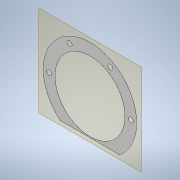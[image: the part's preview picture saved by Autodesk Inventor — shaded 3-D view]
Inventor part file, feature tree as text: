
AUTODESK INVENTOR PART (.ipt)
format: ipt  version: 2020 (Build 240168000, 168)  size: 113,664 bytes
history: native  units: mm
features: other x3, plane x1, extrude x1, sketch x1, reference x1
ambient origin geometry x8: Origin, YZ Plane, XZ Plane, XY Plane, X Axis, Y Axis, Z Axis, Center Point
bodies: 实体1 (feature_tree)
feature tree (7):
  plane  "工作平面1"
  extrude  "拉伸1"  [1 undecoded]
  sketch  "草图1"  dims[d0=0.18mm d1=0.0mm]
  reference  "参考1"
  other  "<userpath>\Desktop\ME_course_project\课设试试\shaft_try_1.iam"
  other  "shaft_try_1.iam"
  other  "轴承端盖3:1"
note: 1 required parameter value undecoded (feature->parameter linkage not recoverable at this tier; creation-order binding heuristic only, values carry confidence <= 0.55)
